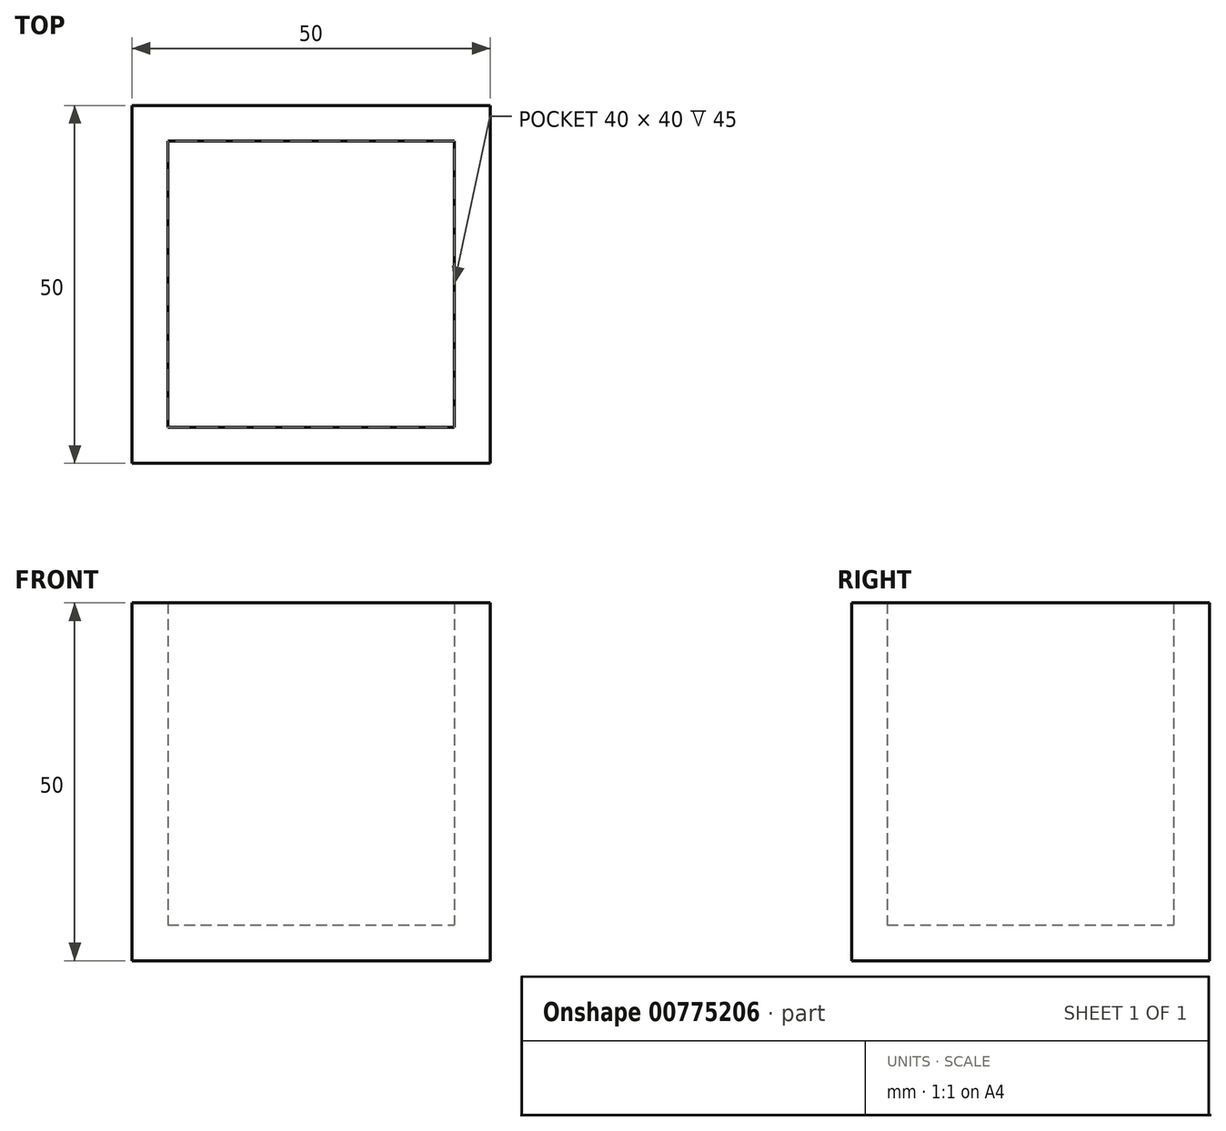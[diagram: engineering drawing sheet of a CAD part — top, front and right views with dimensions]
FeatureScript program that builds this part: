
annotation { "Feature Type Name" : "Feature", "Feature Type Description" : "" }
export const myFeature = defineFeature(function(context is Context, id is Id, definition is map)
    precondition{}
    {
        {
            var Q0;
            Q0=qCreatedBy(makeId("Top.planeOp"),FACE);
            var sketch = newSketch(context, id + "F0", { "sketchPlane" : qUnion([Q0])});
            skLineSegment(sketch, "E0.bottom", {"start": v(-25, -25) * mm, "end": v(25, -25) * mm});
            skLineSegment(sketch, "E0.top", {"start": v(-25, 25) * mm, "end": v(25, 25) * mm});
            skLineSegment(sketch, "E0.left", {"start": v(-25, -25) * mm, "end": v(-25, 25) * mm});
            skLineSegment(sketch, "E0.right", {"start": v(25, -25) * mm, "end": v(25, 25) * mm});
            skPoint(sketch, "E0.middle", {"position": v(0, 0) * mm});
            skLineSegment(sketch, "E1.bottom", {"start": v(-20, -20) * mm, "end": v(20, -20) * mm});
            skLineSegment(sketch, "E1.top", {"start": v(-20, 20) * mm, "end": v(20, 20) * mm});
            skLineSegment(sketch, "E1.left", {"start": v(-20, -20) * mm, "end": v(-20, 20) * mm});
            skLineSegment(sketch, "E1.right", {"start": v(20, -20) * mm, "end": v(20, 20) * mm});
            skSolve(sketch);
        }
        {
            var Q0;
            Q0=makeQuery(id+"F0.imprint","IMPRINT",FACE,{"disambiguationData":[TD([[makeQuery(id+"F0.imprint","IMPRINT",EDGE,{"derivedFrom":sQuery(id+"F0.wireOp",EDGE,"E0.bottom")}),1.0]])]});
            extrude(context, id + "F1", {"entities" : qUnion([Q0]), "depth" : 50 * mm, "offsetDistance" : 25 * mm});
        }
        {
            var Q0;
            Q0=makeQuery(id+"F1.opExtrude","SWEPT_FACE",FACE,{"disambiguationData":[OSD([sQuery(id+"F0.wireOp",EDGE,"E1.top")])]});
            var sketch = newSketch(context, id + "F2", { "sketchPlane" : qUnion([Q0])});
            skLineSegment(sketch, "E2.bottom", {"start": v(-20, 5) * mm, "end": v(20, 5) * mm});
            skLineSegment(sketch, "E2.top", {"start": v(-20, 0) * mm, "end": v(20, 0) * mm});
            skLineSegment(sketch, "E2.left", {"start": v(-20, 5) * mm, "end": v(-20, 0) * mm});
            skLineSegment(sketch, "E2.right", {"start": v(20, 5) * mm, "end": v(20, 0) * mm});
            skSolve(sketch);
        }
        {
            var Q0;
            Q0=makeQuery(id+"F2.imprint","IMPRINT",FACE,{"disambiguationData":[TD([[makeQuery(id+"F2.imprint","IMPRINT",EDGE,{"derivedFrom":sQuery(id+"F2.wireOp",EDGE,"E2.bottom")}),-1.0]])]});
            extrude(context, id + "F3", {"entities" : qUnion([Q0]), "operationType" : NewBodyOperationType.ADD, "depth" : 40 * mm, "offsetDistance" : 25 * mm});
        }
    });
